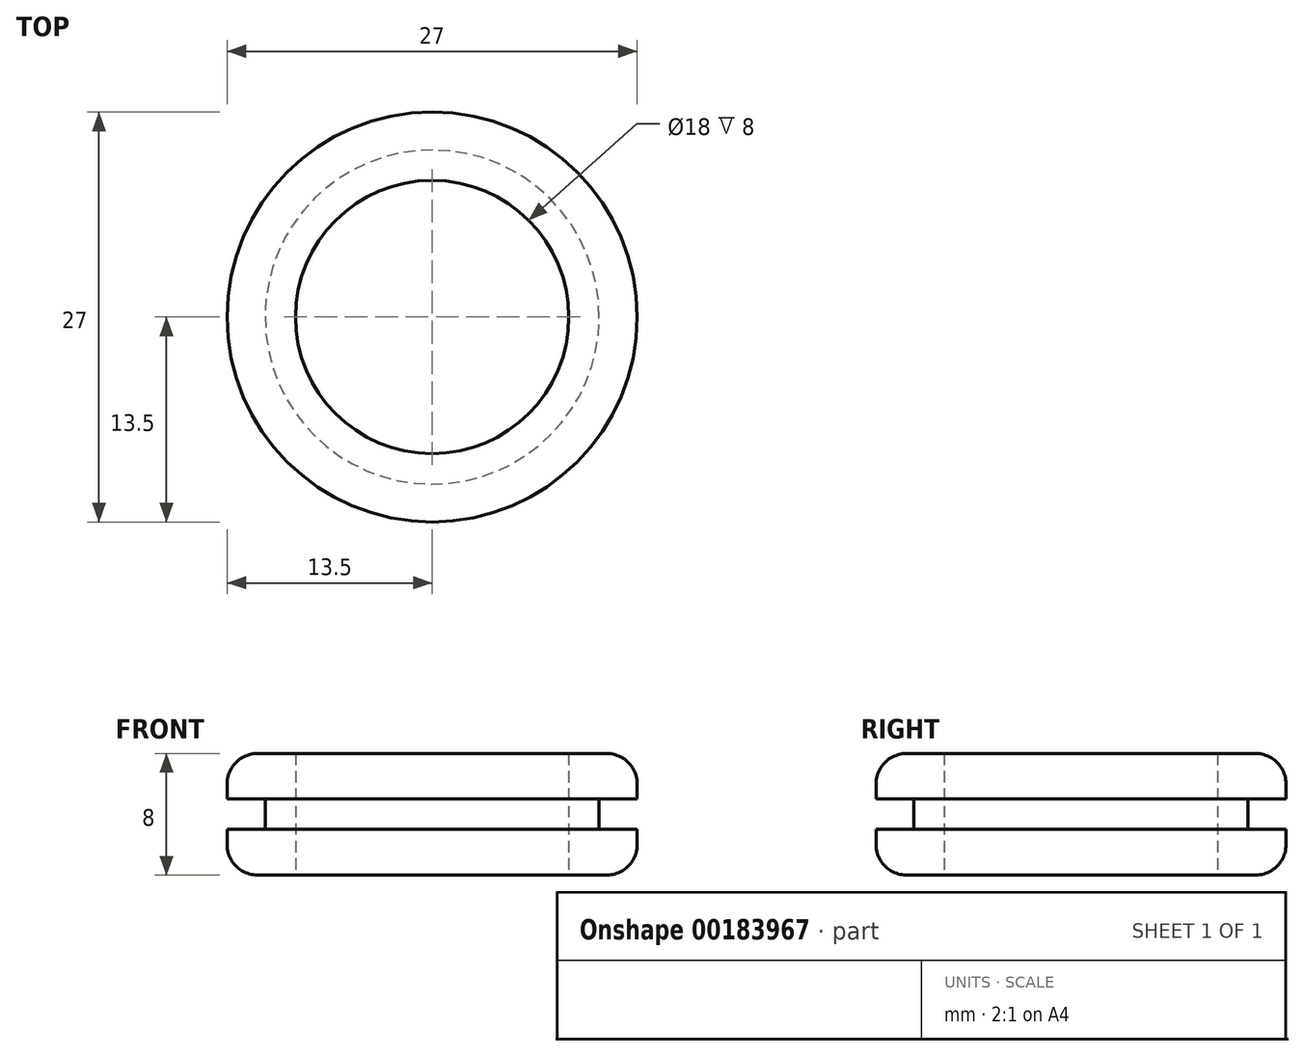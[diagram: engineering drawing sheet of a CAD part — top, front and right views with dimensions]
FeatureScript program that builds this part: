
annotation { "Feature Type Name" : "Feature", "Feature Type Description" : "" }
export const myFeature = defineFeature(function(context is Context, id is Id, definition is map)
    precondition{}
    {
        {
            var Q0;
            Q0=qCreatedBy(makeId("Front.planeOp"),FACE);
            var sketch = newSketch(context, id + "F0", { "sketchPlane" : qUnion([Q0])});
            skLineSegment(sketch, "E0", {"start": v(0, -10.87) * mm, "end": v(0, 9.67) * mm});
            skLineSegment(sketch, "E1", {"start": v(-9, 4) * mm, "end": v(-9, -4) * mm});
            skLineSegment(sketch, "E2", {"start": v(-11, 1) * mm, "end": v(-11, -1) * mm});
            skLineSegment(sketch, "E3", {"start": v(-11, 1) * mm, "end": v(-13.5, 1) * mm});
            skLineSegment(sketch, "E4", {"start": v(-11, -1) * mm, "end": v(-13.5, -1) * mm});
            skLineSegment(sketch, "E5", {"start": v(-9, 4) * mm, "end": v(-11.5, 4) * mm});
            skLineSegment(sketch, "E6", {"start": v(-13.5, 1) * mm, "end": v(-13.5, 2) * mm});
            skLineSegment(sketch, "E7", {"start": v(-9, -4) * mm, "end": v(-11.5, -4) * mm});
            skLineSegment(sketch, "E8", {"start": v(-13.5, -1) * mm, "end": v(-13.5, -2) * mm});
            skPoint(sketch, "E9.visualSharp", {"position": v(-13.5, 4) * mm});
            skArc(sketch, "E9.filletArc", {"start": v(-11.5, 4) * mm, "mid": v(-12.91, 3.41) * mm, "end": v(-13.5, 2) * mm});
            skPoint(sketch, "E10.visualSharp", {"position": v(-13.5, -4) * mm});
            skArc(sketch, "E10.filletArc", {"start": v(-13.5, -2) * mm, "mid": v(-12.91, -3.41) * mm, "end": v(-11.5, -4) * mm});
            skSolve(sketch);
        }
        {
            var Q0;
            Q0=makeQuery(id+"F0.imprint","IMPRINT",FACE,{"disambiguationData":[TD([[makeQuery(id+"F0.imprint","IMPRINT",EDGE,{"derivedFrom":sQuery(id+"F0.wireOp",EDGE,"E1")}),-1.0]])]});
            var Q1;
            Q1=sQuery(id+"F0.wireOp",EDGE,"E0");
            revolve(context, id + "F1", {"entities" : qUnion([Q0]), "axis" : qUnion([Q1]), "revolveType" : RevolveType.FULL});
        }
    });
